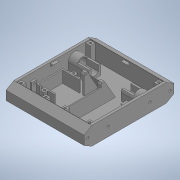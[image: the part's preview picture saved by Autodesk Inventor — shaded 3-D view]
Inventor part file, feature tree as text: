
AUTODESK INVENTOR PART (.ipt)
format: ipt  version: 2020 (Build 240168000, 168)  size: 686,080 bytes
history: native  units: in
note: dims shown in document units (in); Inventor stores cm internally (conversion verified against a paired STEP export)
features: extrude x21, sketch x21, projected_geometry x16, mirror x7, plane x1
ambient origin geometry x8: Origin, YZ Plane, XZ Plane, XY Plane, X Axis, Y Axis, Z Axis, Center Point
bodies: Solid1 (feature_tree)
feature tree (66):
  extrude  "Extrusion1"  Depth=5.9055in
  extrude  "Extrusion2"  TaperAngle=0.0deg  [1 undecoded]
  extrude  "Extrusion3"  Depth=1.063in
  extrude  "Extrusion4"  Depth=0.315in
  extrude  "Extrusion5"  TaperAngle=0.0deg  [1 undecoded]
  extrude  "Extrusion6"  Depth=0.5906in
  mirror  "Mirror1"
  extrude  "Extrusion7"  Depth=0.0787in
  mirror  "Mirror2"
  extrude  "Extrusion8"  Depth=0.6102in
  mirror  "Mirror3"
  plane  "Work Plane1"
  extrude  "Extrusion9"  Depth=0.7874in TaperAngle=0.0deg
  mirror  "Mirror4"
  extrude  "Extrusion10"  Depth=6.063in TaperAngle=0.0deg
  extrude  "Extrusion11"  Depth=0.1575in
  extrude  "Extrusion12"  TaperAngle=0.0deg  [1 undecoded]
  extrude  "Extrusion13"  Depth=0.2756in
  extrude  "Extrusion14"  Depth=0.4331in
  extrude  "Extrusion17"  Depth=2.7559in
  extrude  "Extrusion18"  Depth=0.0453in
  mirror  "Mirror6"
  extrude  "Extrusion19"  TaperAngle=0.0deg  [1 undecoded]
  mirror  "Mirror7"
  extrude  "Extrusion20"  Depth=0.0787in
  extrude  "Extrusion21"  Depth=0.993in
  extrude  "Extrusion22"  Depth=0.2756in
  extrude  "Extrusion23"  Depth=0.4724in
  mirror  "Mirror8"
  sketch  "Sketch1"  dims[d0=1.1811in d1=5.9055in]
  sketch  "Sketch2"  dims[d2=5.1181in d3=0.0in]
  projected_geometry  "Projected Loop1"
  sketch  "Sketch3"  dims[d4=0.1575in d5=1.063in]
  projected_geometry  "Projected Loop2"
  projected_geometry  "Projected Loop3"
  sketch  "Sketch4"  dims[d6=0.0in d8=0.315in]
  sketch  "Sketch5"  dims[d10=0.993in d11=0.0in]
  projected_geometry  "Projected Loop4"
  sketch  "Sketch6"  dims[d12=0.6496in d13=0.5906in]
  sketch  "Sketch7"  dims[d14=1.5748in d15=0.0787in]
  sketch  "Sketch9"  dims[d16=0.5512in d17=0.0in d18=0.6102in]
  sketch  "Sketch10"  dims[d19=0.4803in d20=0.7874in d21=0.0in]
  sketch  "Sketch12"  dims[d22=0.1654in d23=6.063in d24=0.0in]
  projected_geometry  "Projected Loop6"
  projected_geometry  "Projected Loop7"
  projected_geometry  "Projected Loop8"
  sketch  "Sketch13"  dims[d25=0.5114in d26=0.1575in]
  sketch  "Sketch14"  dims[d27=1.5748in d28=0.0in d29=0.0in]
  sketch  "Sketch15"  dims[d30=0.1575in d31=0.2756in]
  projected_geometry  "Projected Loop15"
  sketch  "Sketch16"  dims[d32=0.0in d33=0.4331in]
  projected_geometry  "Projected Loop19"
  projected_geometry  "Projected Loop20"
  projected_geometry  "Projected Loop21"
  projected_geometry  "Projected Loop22"
  projected_geometry  "Projected Loop23"
  projected_geometry  "Projected Loop24"
  sketch  "Sketch20"  dims[d34=0.0906in d38=2.7559in]
  sketch  "Sketch21"  dims[d40=0.0453in d41=0.0909in]
  sketch  "Sketch22"  dims[d42=0.2362in d43=0.0in]
  sketch  "Sketch23"  dims[d44=60.0deg d45=0.0787in]
  sketch  "Sketch25"  dims[d46=0.315in d48=0.993in]
  sketch  "Sketch26"  dims[d49=0.0in d53=0.2756in]
  projected_geometry  "Projected Loop25"
  sketch  "Sketch27"  dims[d54=0.0in d55=0.4724in d56=1.1811in d57=1.5748in d58=1.5748in d59=0.0787in d60=0.0787in d62=0.315in d63=0.7677in d64=0.0in d66=0.1476in d67=0.2756in d68=0.0in d69=0.7874in d70=0.2953in d71=0.1181in d72=0.0in d89=0.0157in d90=0.0157in d91=0.1476in d92=0.1476in d96=0.315in d97=0.1575in d98=0.1181in d99=0.0in d102=0.1772in d104=0.3346in d105=135.0deg d106=0.2362in d107=0.0in d108=0.0394in d109=0.0in d110=0.063in d111=0.0394in d112=0.0in d117=0.993in d118=0.0315in d119=0.3937in d120=0.0in d121=45.0deg d122=0.993in d123=0.1969in d124=0.3937in d125=0.0in d126=45.0deg d127=0.1969in d128=0.993in d129=0.3937in d130=0.0in]
  projected_geometry  "Projected Loop26"
note: 4 required parameter values undecoded (feature->parameter linkage not recoverable at this tier; creation-order binding heuristic only, values carry confidence <= 0.55)
